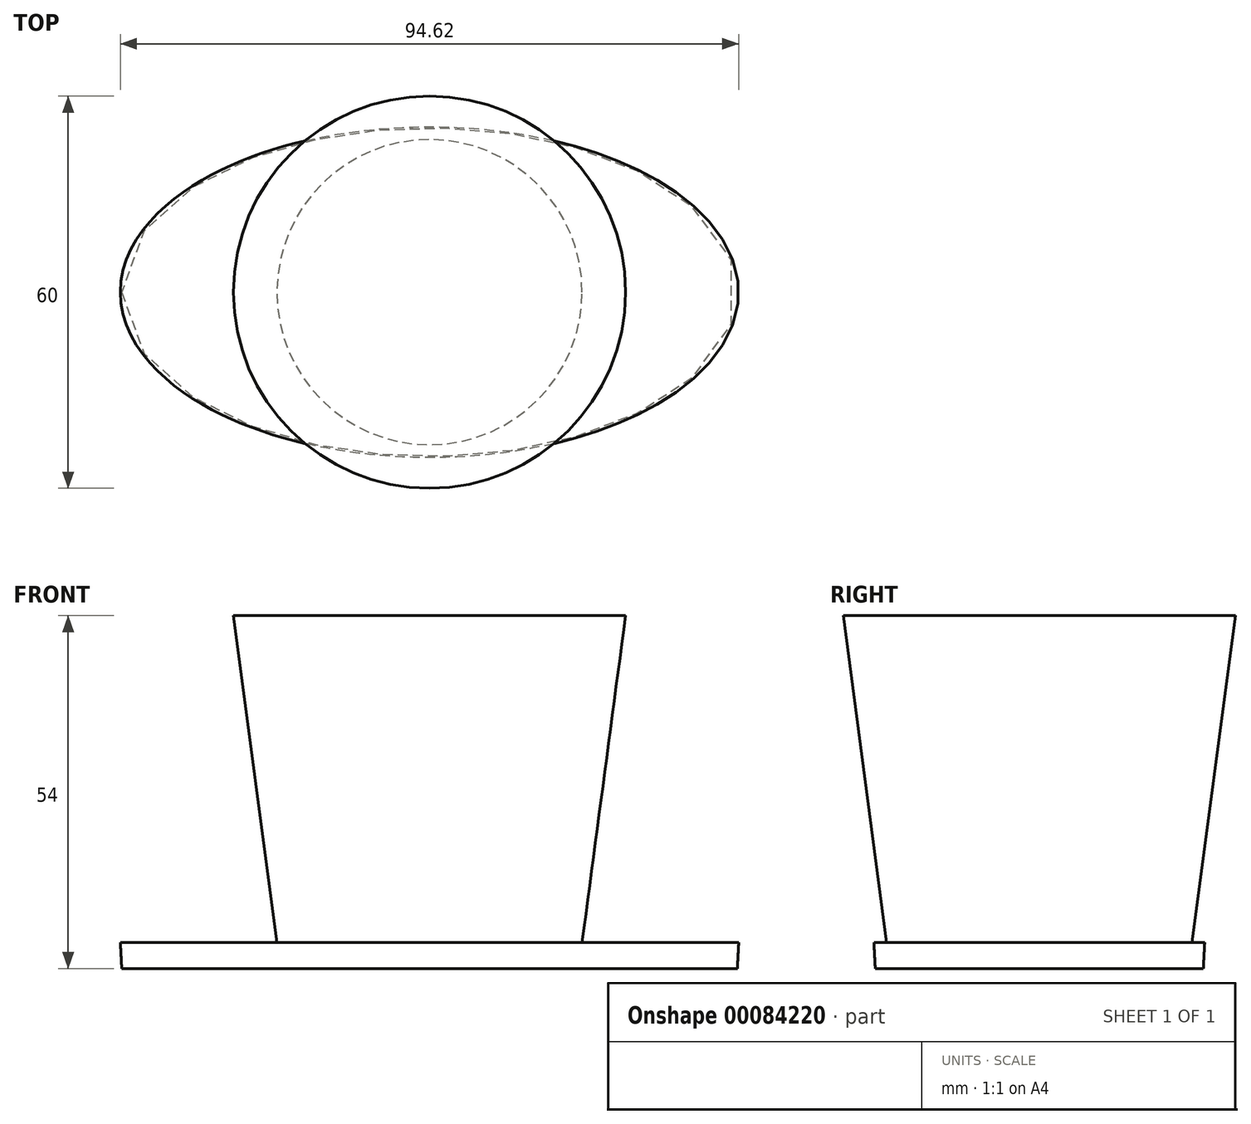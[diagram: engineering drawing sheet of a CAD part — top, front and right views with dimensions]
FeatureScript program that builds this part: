
annotation { "Feature Type Name" : "Feature", "Feature Type Description" : "" }
export const myFeature = defineFeature(function(context is Context, id is Id, definition is map)
    precondition{}
    {
        {
            var Q0;
            Q0=qCreatedBy(makeId("Top.planeOp"),FACE);
            var sketch = newSketch(context, id + "F0", { "sketchPlane" : qUnion([Q0])});
            skEllipse(sketch, "E0", {"center": v(0, 0) * mm, "majorRadius": 47.1 * mm, "minorRadius": 25.1 * mm, "majorAxis": v(1, 0)});
            skSolve(sketch);
        }
        {
            var Q0;
            Q0=makeQuery(id+"F0.imprint","IMPRINT",FACE,{"disambiguationData":[TD([[makeQuery(id+"F0.imprint","IMPRINT",EDGE,{"derivedFrom":sQuery(id+"F0.wireOp",EDGE,"E0")}),1.0]])]});
            extrude(context, id + "F1", {"entities" : qUnion([Q0]), "depth" : 4 * mm, "hasDraft" : true, "draftAngle" : 3 * degree});
        }
        {
            var Q0;
            Q0=makeQuery(id+"F1.opExtrude","CAP_FACE",FACE,{"disambiguationData":[OSD([sQuery(id+"F0.wireOp",EDGE,"E0")])],"isStart":false});
            var sketch = newSketch(context, id + "F2", { "sketchPlane" : qUnion([Q0])});
            skCircle(sketch, "E1", {"center": v(0, 0) * mm, "radius": 23.35 * mm});
            skSolve(sketch);
        }
        {
            var Q0;
            Q0=makeQuery(id+"F2.imprint","IMPRINT",FACE,{"disambiguationData":[TD([[makeQuery(id+"F2.imprint","IMPRINT",EDGE,{"derivedFrom":sQuery(id+"F2.wireOp",EDGE,"E1")}),-1.0]])]});
            cPlane(context, id + "F3", {"entities" : qUnion([Q0]), "cplaneType" : CPlaneType.OFFSET, "offset" : 50 * mm, "width" : 152.4 * mm, "height" : 152.4 * mm});
        }
        {
            var Q0;
            Q0=qCreatedBy(id+"F3.planeOp",FACE);
            var sketch = newSketch(context, id + "F4", { "sketchPlane" : qUnion([Q0])});
            skCircle(sketch, "E2", {"center": v(0, 0) * mm, "radius": 30 * mm});
            skSolve(sketch);
        }
        {
            var Q0;
            Q0=makeQuery(id+"F4.imprint","IMPRINT",FACE,{"disambiguationData":[TD([[makeQuery(id+"F4.imprint","IMPRINT",EDGE,{"derivedFrom":sQuery(id+"F4.wireOp",EDGE,"E2")}),1.0]])]});
            var Q1;
            Q1=makeQuery(id+"F2.imprint","IMPRINT",FACE,{"disambiguationData":[TD([[makeQuery(id+"F2.imprint","IMPRINT",EDGE,{"derivedFrom":sQuery(id+"F2.wireOp",EDGE,"E1")}),1.0]])]});
            var Q2;
            Q2=sQuery(id+"F2.wireOp",EDGE,"E1");
            var Q3;
            Q3=sQuery(id+"F4.wireOp",EDGE,"E2");
            loft(context, id + "F5", {"sheetProfilesArray" : [{ "sheetProfileEntities" : qUnion([Q0]) }, { "sheetProfileEntities" : qUnion([Q1]) }], "wireProfilesArray" : [{ "wireProfileEntities" : qUnion([Q2]) }, { "wireProfileEntities" : qUnion([Q3]) }]});
        }
    });
